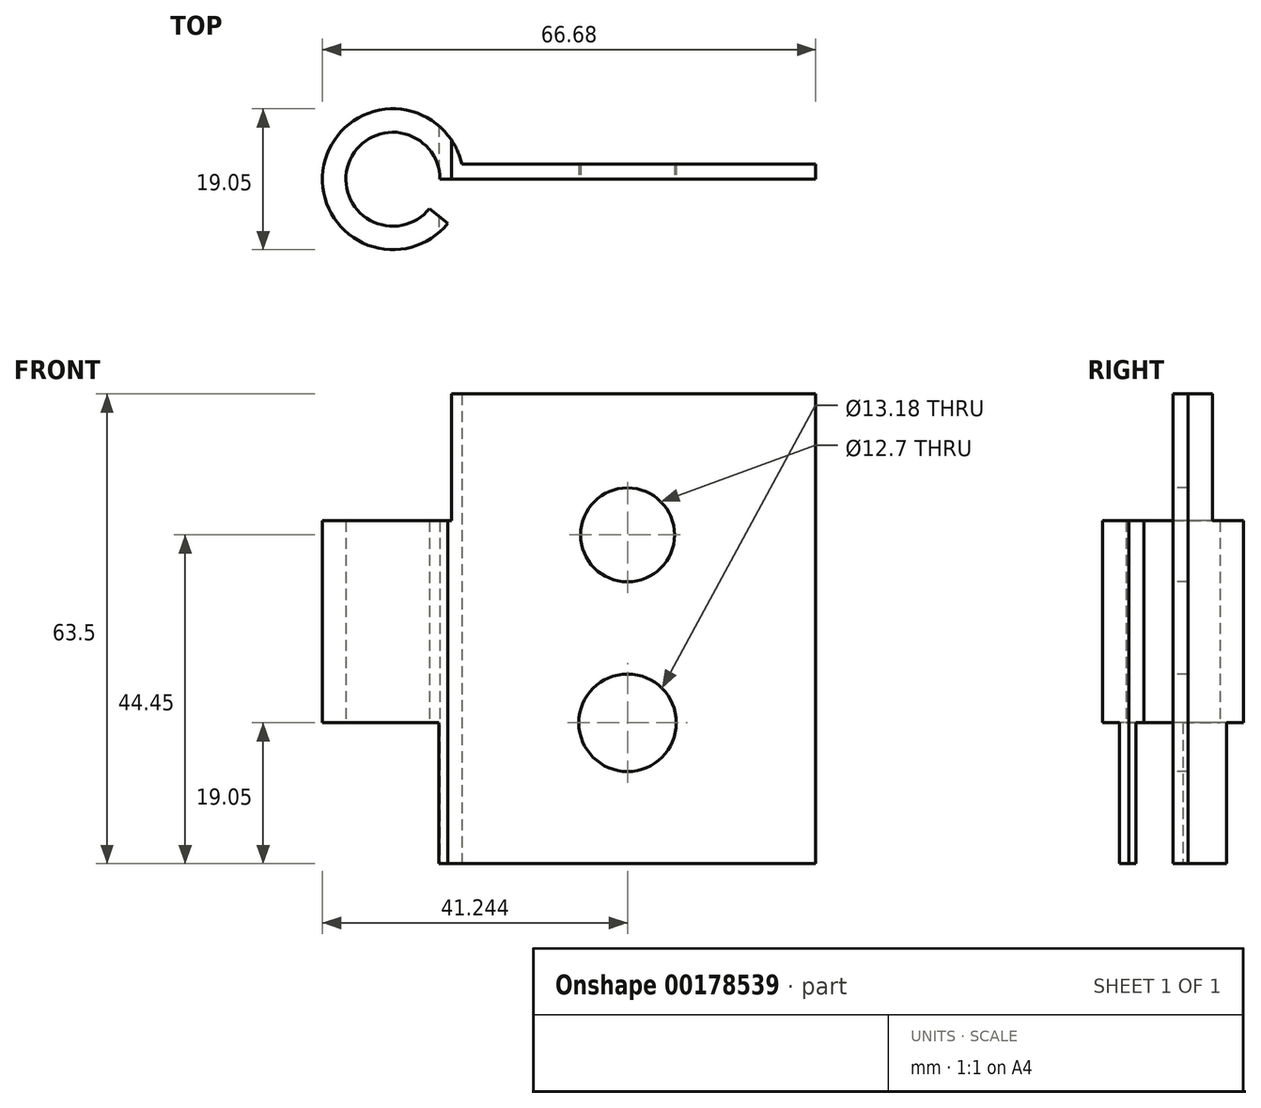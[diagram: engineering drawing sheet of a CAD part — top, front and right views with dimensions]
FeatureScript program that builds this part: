
annotation { "Feature Type Name" : "Feature", "Feature Type Description" : "" }
export const myFeature = defineFeature(function(context is Context, id is Id, definition is map)
    precondition{}
    {
        {
            var Q0;
            Q0=qCreatedBy(makeId("Top.planeOp"),FACE);
            var sketch = newSketch(context, id + "F0", { "sketchPlane" : qUnion([Q0])});
            skArc(sketch, "E0", {"start": v(6.35, 0) * mm, "mid": v(-6, 2.1) * mm, "end": v(4.97, -3.96) * mm});
            skArc(sketch, "E1", {"start": v(9.3, 2.06) * mm, "mid": v(-9.27, 2.18) * mm, "end": v(7.41, -5.98) * mm});
            skLineSegment(sketch, "E2", {"start": v(6.35, 0) * mm, "end": v(57.15, 0) * mm});
            skLineSegment(sketch, "E3", {"start": v(57.15, 0) * mm, "end": v(57.15, 2.06) * mm});
            skLineSegment(sketch, "E4", {"start": v(57.15, 2.06) * mm, "end": v(9.3, 2.06) * mm});
            skLineSegment(sketch, "E5", {"start": v(4.97, -3.96) * mm, "end": v(7.41, -5.98) * mm});
            skLineSegment(sketch, "E6", {"start": v(7.41, -5.98) * mm, "end": v(7.41, -5.98) * mm});
            skLineSegment(sketch, "E7", {"start": v(7.41, -5.98) * mm, "end": v(4.97, -3.96) * mm});
            skSolve(sketch);
        }
        {
            var Q0;
            Q0 = qSketchRegion(id + "F0", true);
            extrude(context, id + "F1", {"entities" : qUnion([Q0]), "depth" : 63.5 * mm});
        }
        {
            var Q0;
            Q0=makeQuery(id+"F1.opExtrude","SWEPT_FACE",FACE,{"disambiguationData":[OSD([sQuery(id+"F0.wireOp",EDGE,"E2")])]});
            var sketch = newSketch(context, id + "F2", { "sketchPlane" : qUnion([Q0])});
            skCircle(sketch, "E8", {"center": v(31.71, 44.45) * mm, "radius": 6.35 * mm});
            skCircle(sketch, "E9", {"center": v(31.71, 19.05) * mm, "radius": 6.59 * mm});
            skSolve(sketch);
        }
        {
            var Q0;
            Q0=makeQuery(id+"F2.imprint","IMPRINT",FACE,{"disambiguationData":[TD([[makeQuery(id+"F2.imprint","IMPRINT",EDGE,{"derivedFrom":sQuery(id+"F2.wireOp",EDGE,"E8")}),1.0]])]});
            var Q1;
            Q1=makeQuery(id+"F2.imprint","IMPRINT",FACE,{"disambiguationData":[TD([[makeQuery(id+"F2.imprint","IMPRINT",EDGE,{"derivedFrom":sQuery(id+"F2.wireOp",EDGE,"E9")}),1.0]])]});
            extrude(context, id + "F3", {"entities" : qUnion([Q0, Q1]), "operationType" : NewBodyOperationType.REMOVE, "endBound" : BoundingType.THROUGH_ALL, "oppositeDirection" : true, "depth" : 25.4 * mm});
        }
        {
            var Q0;
            Q0=makeQuery(id+"F2.imprint","IMPRINT",FACE,{"disambiguationData":[TD([[makeQuery(id+"F2.imprint","IMPRINT",EDGE,{"derivedFrom":sQuery(id+"F2.wireOp",EDGE,"E8")}),-1.0]])]});
            var sketch = newSketch(context, id + "F4", { "sketchPlane" : qUnion([Q0])});
            skLineSegment(sketch, "E10", {"start": v(6.2, 0) * mm, "end": v(-23.1, 0) * mm});
            skLineSegment(sketch, "E11", {"start": v(7.9, 65.41) * mm, "end": v(-20.53, 65.41) * mm});
            skLineSegment(sketch, "E12", {"start": v(7.9, 46.36) * mm, "end": v(-20.53, 46.36) * mm});
            skLineSegment(sketch, "E13", {"start": v(6.2, 19.05) * mm, "end": v(-23.1, 19.05) * mm});
            skLineSegment(sketch, "E14", {"start": v(7.9, 65.41) * mm, "end": v(7.9, 46.36) * mm});
            skLineSegment(sketch, "E15", {"start": v(-20.53, 65.41) * mm, "end": v(-20.53, 46.36) * mm});
            skLineSegment(sketch, "E16", {"start": v(6.2, 19.05) * mm, "end": v(6.2, 0) * mm});
            skLineSegment(sketch, "E17", {"start": v(-23.1, 19.05) * mm, "end": v(-23.1, 0) * mm});
            skSolve(sketch);
        }
        {
            var Q0;
            Q0 = qSketchRegion(id + "F4", true);
            extrude(context, id + "F5", {"entities" : qUnion([Q0]), "operationType" : NewBodyOperationType.REMOVE, "endBound" : BoundingType.SYMMETRIC, "oppositeDirection" : true, "depth" : 25.4 * mm});
        }
    });
